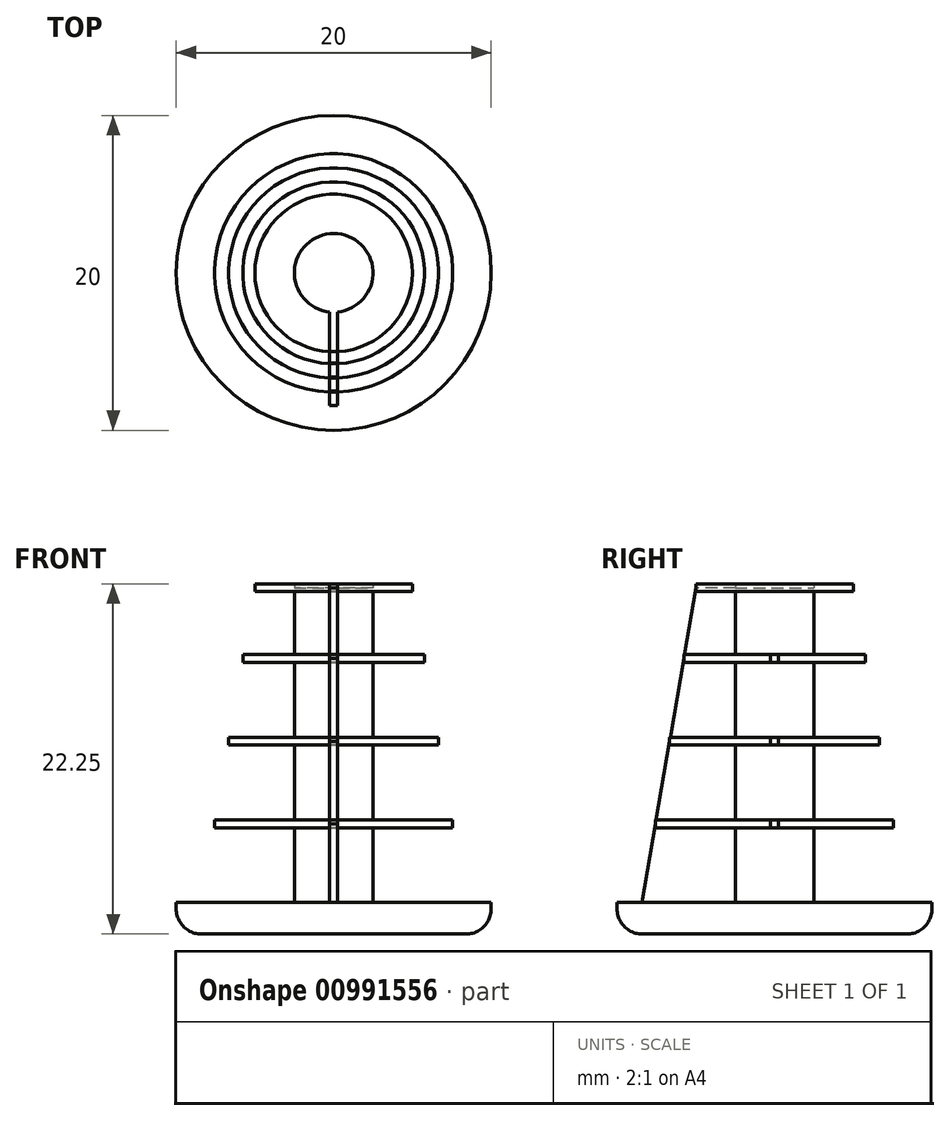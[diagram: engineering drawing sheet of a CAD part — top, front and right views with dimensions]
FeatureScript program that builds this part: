
annotation { "Feature Type Name" : "Feature", "Feature Type Description" : "" }
export const myFeature = defineFeature(function(context is Context, id is Id, definition is map)
    precondition{}
    {
        {
            var Q0;
            Q0=qCreatedBy(makeId("Top.planeOp"),FACE);
            var sketch = newSketch(context, id + "F0", { "sketchPlane" : qUnion([Q0])});
            skCircle(sketch, "E0", {"center": v(0, 0) * mm, "radius": 10 * mm});
            skSolve(sketch);
        }
        {
            var Q0;
            Q0=makeQuery(id+"F0.imprint","IMPRINT",FACE,{"disambiguationData":[TD([[makeQuery(id+"F0.imprint","IMPRINT",EDGE,{"derivedFrom":sQuery(id+"F0.wireOp",EDGE,"E0")}),1.0]])]});
            extrude(context, id + "F1", {"entities" : qUnion([Q0]), "depth" : 2 * mm, "offsetDistance" : 25 * mm});
        }
        {
            var Q0;
            Q0=makeQuery(id+"F1.opExtrude","CAP_EDGE",EDGE,{"disambiguationData":[OSD([sQuery(id+"F0.wireOp",EDGE,"E0")])],"isStart":true});
            fillet(context, id + "F2", {"entities" : qUnion([Q0]), "radius" : 1.6 * mm, "tangentPropagation" : true, "allowEdgeOverflow" : false});
        }
        {
            var Q0;
            Q0=makeQuery(id+"F1.opExtrude","CAP_FACE",FACE,{"disambiguationData":[OSD([sQuery(id+"F0.wireOp",EDGE,"E0")])],"isStart":false});
            var sketch = newSketch(context, id + "F3", { "sketchPlane" : qUnion([Q0])});
            skCircle(sketch, "E1", {"center": v(0, 0) * mm, "radius": 2.5 * mm});
            skSolve(sketch);
        }
        {
            var Q0;
            Q0=makeQuery(id+"F3.imprint","IMPRINT",FACE,{"disambiguationData":[TD([[makeQuery(id+"F3.imprint","IMPRINT",EDGE,{"derivedFrom":sQuery(id+"F3.wireOp",EDGE,"E1")}),1.0]])]});
            extrude(context, id + "F4", {"entities" : qUnion([Q0]), "operationType" : NewBodyOperationType.ADD, "depth" : 20 * mm, "offsetDistance" : 25 * mm});
        }
        {
            var Q0;
            Q0=qCreatedBy(makeId("Right.planeOp"),FACE);
            var sketch = newSketch(context, id + "F5", { "sketchPlane" : qUnion([Q0])});
            skLineSegment(sketch, "E2", {"start": v(2.5, 22) * mm, "end": v(2.5, 2) * mm});
            skLineSegment(sketch, "E3", {"start": v(-2.5, 2) * mm, "end": v(-2.5, 22) * mm});
            skLineSegment(sketch, "E4", {"start": v(10, 2) * mm, "end": v(10, 1.6) * mm});
            skLineSegment(sketch, "E5", {"start": v(-10, 1.6) * mm, "end": v(-10, 2) * mm});
            skLineSegment(sketch, "E6", {"start": v(-1.5, 22) * mm, "end": v(-5, 22) * mm});
            skLineSegment(sketch, "E7", {"start": v(-5, 22) * mm, "end": v(-8.5, 1.5) * mm});
            skLineSegment(sketch, "E8", {"start": v(-8.5, 1.5) * mm, "end": v(-1.5, 1.5) * mm});
            skLineSegment(sketch, "E9", {"start": v(-1.5, 1.5) * mm, "end": v(-1.5, 22) * mm});
            skSolve(sketch);
        }
        {
            var Q0;
            {var subQ0=sQuery(id+"F5.wireOp",EDGE,"E7");Q0=makeQuery(id+"F5.imprint","IMPRINT",FACE,{"disambiguationData":[TD([[makeQuery(id+"F5.imprint","IMPRINT",EDGE,{"derivedFrom":subQ0}),1.0]])]});}
            extrude(context, id + "F6", {"entities" : qUnion([Q0]), "operationType" : NewBodyOperationType.ADD, "depth" : 0.5 * mm, "offsetDistance" : 25 * mm, "symmetric" : true});
        }
        {
            var Q0;
            Q0=makeQuery(id+"F1.opExtrude","CAP_FACE",FACE,{"disambiguationData":[OSD([sQuery(id+"F0.wireOp",EDGE,"E0")])],"isStart":false});
            cPlane(context, id + "F7", {"entities" : qUnion([Q0]), "cplaneType" : CPlaneType.OFFSET, "offset" : 5 * mm, "width" : 150 * mm, "height" : 150 * mm});
        }
        {
            var Q0;
            Q0=qCreatedBy(id+"F7.planeOp",FACE);
            var sketch = newSketch(context, id + "F8", { "sketchPlane" : qUnion([Q0])});
            skLineSegment(sketch, "E10", {"start": v(0.25, -7.56) * mm, "end": v(-0.25, -7.56) * mm});
            skLineSegment(sketch, "E11", {"start": v(7.56, 0.25) * mm, "end": v(7.56, -0.25) * mm});
            skLineSegment(sketch, "E12", {"start": v(-0.25, 7.56) * mm, "end": v(0.25, 7.56) * mm});
            skLineSegment(sketch, "E13", {"start": v(-7.56, -0.25) * mm, "end": v(-7.56, 0.25) * mm});
            skCircle(sketch, "E14", {"center": v(0, 0) * mm, "radius": 7.57 * mm});
            skSolve(sketch);
        }
        {
            var Q0;
            {var subQ3=sQuery(id+"F8.wireOp",EDGE,"E10");Q0=makeQuery(id+"F8.imprint","IMPRINT",FACE,{"disambiguationData":[TD([[makeQuery(id+"F8.imprint","IMPRINT",EDGE,{"derivedFrom":subQ3}),-1.0]])]});}
            extrude(context, id + "F9", {"entities" : qUnion([Q0]), "operationType" : NewBodyOperationType.ADD, "depth" : 0.5 * mm, "offsetDistance" : 25 * mm, "symmetric" : true});
        }
        {
            var Q0;
            Q0=makeQuery(id+"F9.opExtrude","CAP_FACE",FACE,{"disambiguationData":[OSD([sQuery(id+"F8.wireOp",EDGE,"E10"),sQuery(id+"F8.wireOp",EDGE,"E11"),sQuery(id+"F8.wireOp",EDGE,"E12"),sQuery(id+"F8.wireOp",EDGE,"E13"),sQuery(id+"F8.wireOp",EDGE,"E14")])],"isStart":false});
            cPlane(context, id + "F10", {"entities" : qUnion([Q0]), "cplaneType" : CPlaneType.OFFSET, "offset" : 5 * mm, "width" : 150 * mm, "height" : 150 * mm});
        }
        {
            var Q0;
            Q0=qCreatedBy(id+"F10.planeOp",FACE);
            var sketch = newSketch(context, id + "F11", { "sketchPlane" : qUnion([Q0])});
            skLineSegment(sketch, "E15", {"start": v(6.66, 0.25) * mm, "end": v(6.66, -0.25) * mm});
            skLineSegment(sketch, "E16", {"start": v(0.25, -6.66) * mm, "end": v(-0.25, -6.66) * mm});
            skLineSegment(sketch, "E17", {"start": v(-0.25, 6.66) * mm, "end": v(0.25, 6.66) * mm});
            skLineSegment(sketch, "E18", {"start": v(-6.66, -0.25) * mm, "end": v(-6.66, 0.25) * mm});
            skCircle(sketch, "E19", {"center": v(0, 0) * mm, "radius": 6.67 * mm});
            skSolve(sketch);
        }
        {
            var Q0;
            {var subQ3=sQuery(id+"F11.wireOp",EDGE,"E15");Q0=makeQuery(id+"F11.imprint","IMPRINT",FACE,{"disambiguationData":[TD([[makeQuery(id+"F11.imprint","IMPRINT",EDGE,{"derivedFrom":subQ3}),-1.0]])]});}
            extrude(context, id + "F12", {"entities" : qUnion([Q0]), "operationType" : NewBodyOperationType.ADD, "depth" : 0.5 * mm, "offsetDistance" : 25 * mm, "symmetric" : true});
        }
        {
            var Q0;
            Q0=makeQuery(id+"F12.opExtrude","CAP_FACE",FACE,{"disambiguationData":[OSD([sQuery(id+"F11.wireOp",EDGE,"E15"),sQuery(id+"F11.wireOp",EDGE,"E16"),sQuery(id+"F11.wireOp",EDGE,"E17"),sQuery(id+"F11.wireOp",EDGE,"E18"),sQuery(id+"F11.wireOp",EDGE,"E19")])],"isStart":false});
            cPlane(context, id + "F13", {"entities" : qUnion([Q0]), "cplaneType" : CPlaneType.OFFSET, "offset" : 5 * mm, "width" : 150 * mm, "height" : 150 * mm});
        }
        {
            var Q0;
            Q0=qCreatedBy(id+"F13.planeOp",FACE);
            var sketch = newSketch(context, id + "F14", { "sketchPlane" : qUnion([Q0])});
            skLineSegment(sketch, "E20", {"start": v(0.25, -5.77) * mm, "end": v(-0.25, -5.77) * mm});
            skLineSegment(sketch, "E21", {"start": v(5.77, 0.25) * mm, "end": v(5.77, -0.25) * mm});
            skLineSegment(sketch, "E22", {"start": v(-0.25, 5.77) * mm, "end": v(0.25, 5.77) * mm});
            skLineSegment(sketch, "E23", {"start": v(-5.77, -0.25) * mm, "end": v(-5.77, 0.25) * mm});
            skCircle(sketch, "E24", {"center": v(0, 0) * mm, "radius": 5.77 * mm});
            skSolve(sketch);
        }
        {
            var Q0;
            {var subQ3=sQuery(id+"F14.wireOp",EDGE,"E20");Q0=makeQuery(id+"F14.imprint","IMPRINT",FACE,{"disambiguationData":[TD([[makeQuery(id+"F14.imprint","IMPRINT",EDGE,{"derivedFrom":subQ3}),-1.0]])]});}
            extrude(context, id + "F15", {"entities" : qUnion([Q0]), "operationType" : NewBodyOperationType.ADD, "depth" : 0.5 * mm, "offsetDistance" : 25 * mm, "symmetric" : true});
        }
        {
            var Q0;
            {var subQ0=sQuery(id+"F5.wireOp",EDGE,"E6");Q0=makeQuery(id+"FKaFkKLsK9sWWym_1.3.F6.boolean.opBoolean","MERGE",FACE,{"derivedFrom":[makeQuery(id+"FKaFkKLsK9sWWym_1.2.F6.boolean.opBoolean","MERGE",FACE,{"derivedFrom":[makeQuery(id+"FKaFkKLsK9sWWym_1.1.F6.boolean.opBoolean","MERGE",FACE,{"derivedFrom":[makeQuery(id+"F6.boolean.opBoolean","MERGE",FACE,{"derivedFrom":[makeQuery(id+"F4.opExtrude","CAP_FACE",FACE,{"disambiguationData":[OSD([sQuery(id+"F3.wireOp",EDGE,"E1")])],"isStart":false}),makeQuery(id+"F6.opExtrude","SWEPT_FACE",FACE,{"disambiguationData":[OSD([subQ0])]})]}),makeQuery(id+"FKaFkKLsK9sWWym_1.1.F6.opExtrude","SWEPT_FACE",FACE,{"disambiguationData":[OSD([subQ0])]})]}),makeQuery(id+"FKaFkKLsK9sWWym_1.2.F6.opExtrude","SWEPT_FACE",FACE,{"disambiguationData":[OSD([subQ0])]})]}),makeQuery(id+"FKaFkKLsK9sWWym_1.3.F6.opExtrude","SWEPT_FACE",FACE,{"disambiguationData":[OSD([subQ0])]})]});}
            var sketch = newSketch(context, id + "F16", { "sketchPlane" : qUnion([Q0])});
            skCircle(sketch, "E25", {"center": v(0, 0) * mm, "radius": 5 * mm});
            skLineSegment(sketch, "E26", {"start": v(-0.25, 5) * mm, "end": v(0.25, 5) * mm});
            skSolve(sketch);
        }
        {
            var Q0;
            {var subQ1=sQuery(id+"F5.wireOp",EDGE,"E6");var subQ2=makeQuery(id+"F6.opExtrude","CAP_EDGE",EDGE,{"disambiguationData":[OSD([subQ1])],"isStart":true});Q0=makeQuery(id+"F16.imprint","IMPRINT",FACE,{"disambiguationData":[TD([[makeQuery(id+"F16.imprint","IMPRINT",EDGE,{"derivedFrom":subQ2}),-1.0]])]});}
            var Q1;
            {var subQ1=sQuery(id+"F5.wireOp",EDGE,"E6");var subQ2=makeQuery(id+"FKaFkKLsK9sWWym_1.1.F6.opExtrude","CAP_EDGE",EDGE,{"disambiguationData":[OSD([subQ1])],"isStart":true});Q1=makeQuery(id+"F16.imprint","IMPRINT",FACE,{"disambiguationData":[TD([[makeQuery(id+"F16.imprint","IMPRINT",EDGE,{"derivedFrom":subQ2}),-1.0]])]});}
            var Q2;
            {var subQ1=sQuery(id+"F5.wireOp",EDGE,"E6");var subQ2=makeQuery(id+"FKaFkKLsK9sWWym_1.2.F6.opExtrude","CAP_EDGE",EDGE,{"disambiguationData":[OSD([subQ1])],"isStart":true});Q2=makeQuery(id+"F16.imprint","IMPRINT",FACE,{"disambiguationData":[TD([[makeQuery(id+"F16.imprint","IMPRINT",EDGE,{"derivedFrom":subQ2}),-1.0]])]});}
            var Q3;
            {var subQ1=sQuery(id+"F5.wireOp",EDGE,"E6");var subQ2=makeQuery(id+"F6.opExtrude","CAP_EDGE",EDGE,{"disambiguationData":[OSD([subQ1])],"isStart":false});Q3=makeQuery(id+"F16.imprint","IMPRINT",FACE,{"disambiguationData":[TD([[makeQuery(id+"F16.imprint","IMPRINT",EDGE,{"derivedFrom":subQ2}),1.0]])]});}
            var Q4;
            Q4=makeQuery(id+"F16.imprint","IMPRINT",FACE,{"disambiguationData":[TD([[makeQuery(id+"F16.imprint","IMPRINT",EDGE,{"derivedFrom":sQuery(id+"F16.wireOp",EDGE,"E26")}),-1.0]])]});
            extrude(context, id + "F17", {"entities" : qUnion([Q0, Q1, Q2, Q3, Q4]), "operationType" : NewBodyOperationType.ADD, "depth" : 0.5 * mm, "offsetDistance" : 25 * mm, "symmetric" : true});
        }
    });
